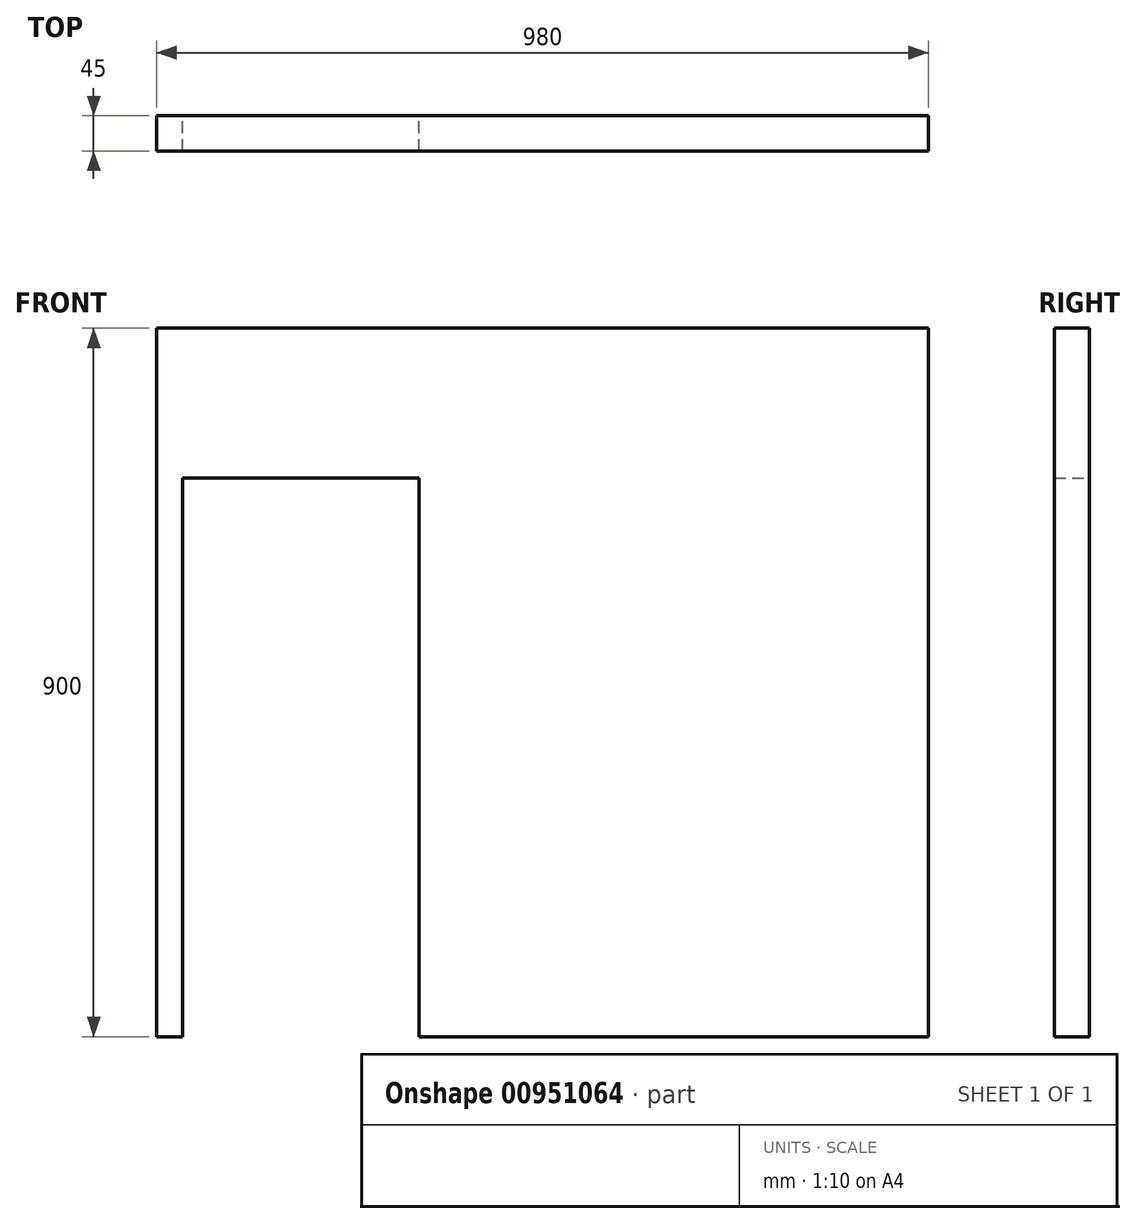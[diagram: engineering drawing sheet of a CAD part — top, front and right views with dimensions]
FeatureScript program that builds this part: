
annotation { "Feature Type Name" : "Feature", "Feature Type Description" : "" }
export const myFeature = defineFeature(function(context is Context, id is Id, definition is map)
    precondition{}
    {
        {
            var Q0;
            Q0=qCreatedBy(makeId("Front.planeOp"),FACE);
            var sketch = newSketch(context, id + "F0", { "sketchPlane" : qUnion([Q0])});
            skLineSegment(sketch, "E0.bottom", {"start": v(490, 450) * mm, "end": v(-490, 450) * mm});
            skLineSegment(sketch, "E0.top", {"start": v(490, -450) * mm, "end": v(-490, -450) * mm});
            skLineSegment(sketch, "E0.left", {"start": v(490, 450) * mm, "end": v(490, -450) * mm});
            skLineSegment(sketch, "E0.right", {"start": v(-490, 450) * mm, "end": v(-490, -450) * mm});
            skPoint(sketch, "E0.middle", {"position": v(0, 0) * mm});
            skLineSegment(sketch, "E1", {"start": v(-157, 260) * mm, "end": v(-457, 260) * mm});
            skLineSegment(sketch, "E2", {"start": v(-457, 260) * mm, "end": v(-457, -450) * mm});
            skLineSegment(sketch, "E3", {"start": v(-157, 260) * mm, "end": v(-157, -450) * mm});
            skSolve(sketch);
        }
        {
            var Q0;
            Q0=makeQuery(id+"F0.imprint","IMPRINT",FACE,{"disambiguationData":[TD([[makeQuery(id+"F0.imprint","IMPRINT",EDGE,{"derivedFrom":sQuery(id+"F0.wireOp",EDGE,"E0.bottom")}),1.0]])]});
            extrude(context, id + "F1", {"entities" : qUnion([Q0]), "endBound" : BoundingType.SYMMETRIC, "depth" : 45 * mm, "offsetDistance" : 25 * mm});
        }
    });
